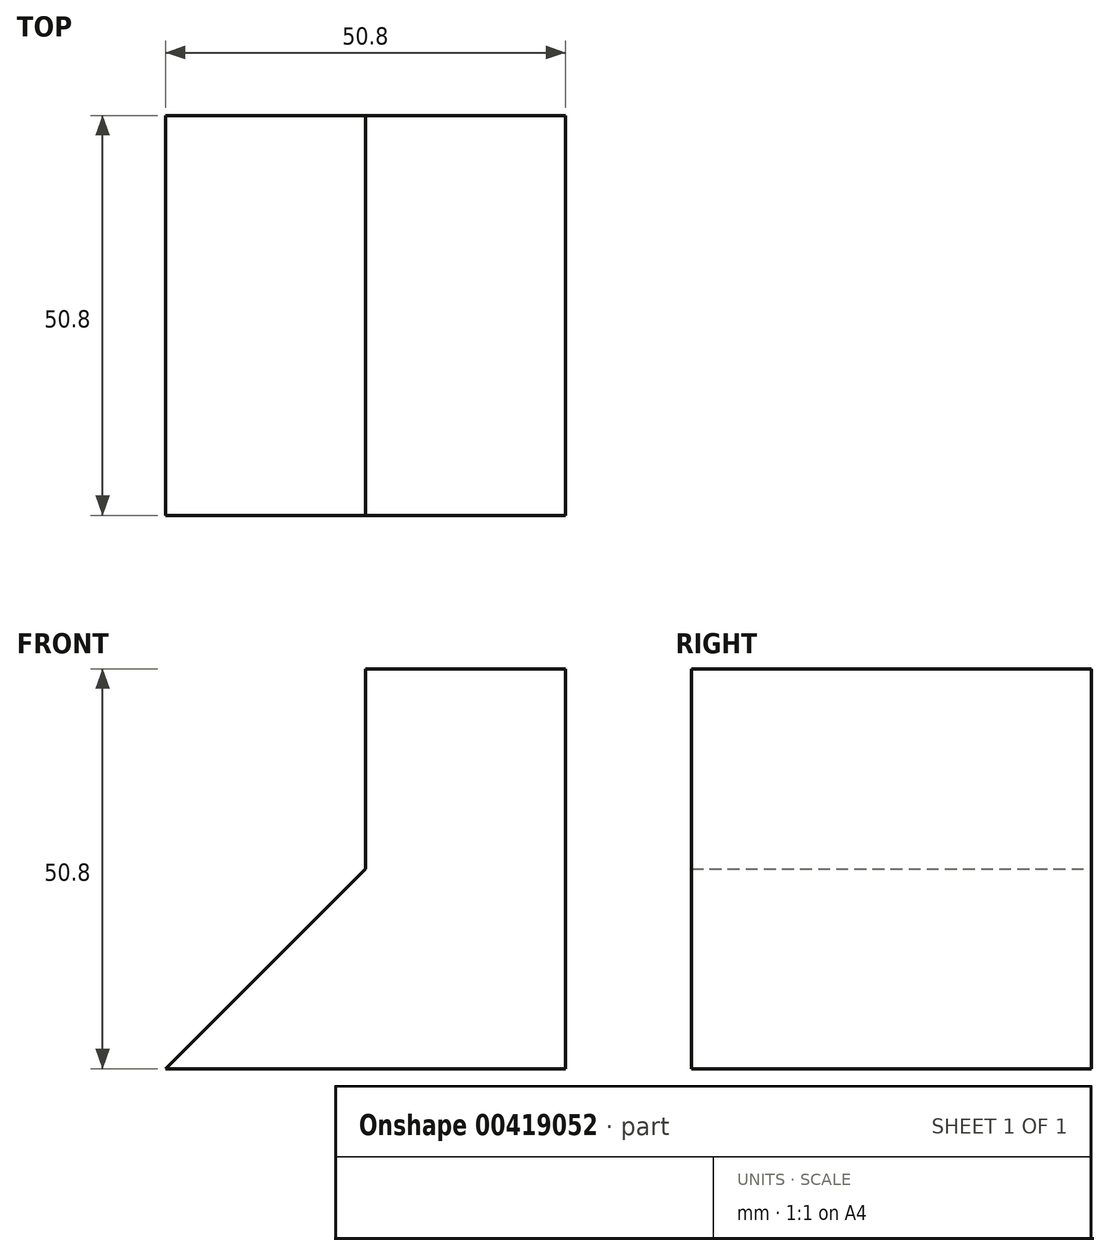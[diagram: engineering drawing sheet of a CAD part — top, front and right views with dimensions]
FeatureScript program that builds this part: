
annotation { "Feature Type Name" : "Feature", "Feature Type Description" : "" }
export const myFeature = defineFeature(function(context is Context, id is Id, definition is map)
    precondition{}
    {
        {
            var Q0;
            Q0=qCreatedBy(makeId("Front.planeOp"),FACE);
            var sketch = newSketch(context, id + "F0", { "sketchPlane" : qUnion([Q0])});
            skLineSegment(sketch, "E0", {"start": v(0, 0) * mm, "end": v(-50.8, 0) * mm});
            skLineSegment(sketch, "E1", {"start": v(0, 0) * mm, "end": v(0, 50.8) * mm});
            skLineSegment(sketch, "E2", {"start": v(0, 50.8) * mm, "end": v(-25.4, 50.8) * mm});
            skLineSegment(sketch, "E3", {"start": v(-25.4, 50.8) * mm, "end": v(-25.4, 25.4) * mm});
            skLineSegment(sketch, "E4", {"start": v(-25.4, 25.4) * mm, "end": v(-50.8, 0) * mm});
            skSolve(sketch);
        }
        {
            var Q0;
            Q0 = qSketchRegion(id + "F0", true);
            extrude(context, id + "F1", {"entities" : qUnion([Q0]), "depth" : 50.8 * mm});
        }
    });
